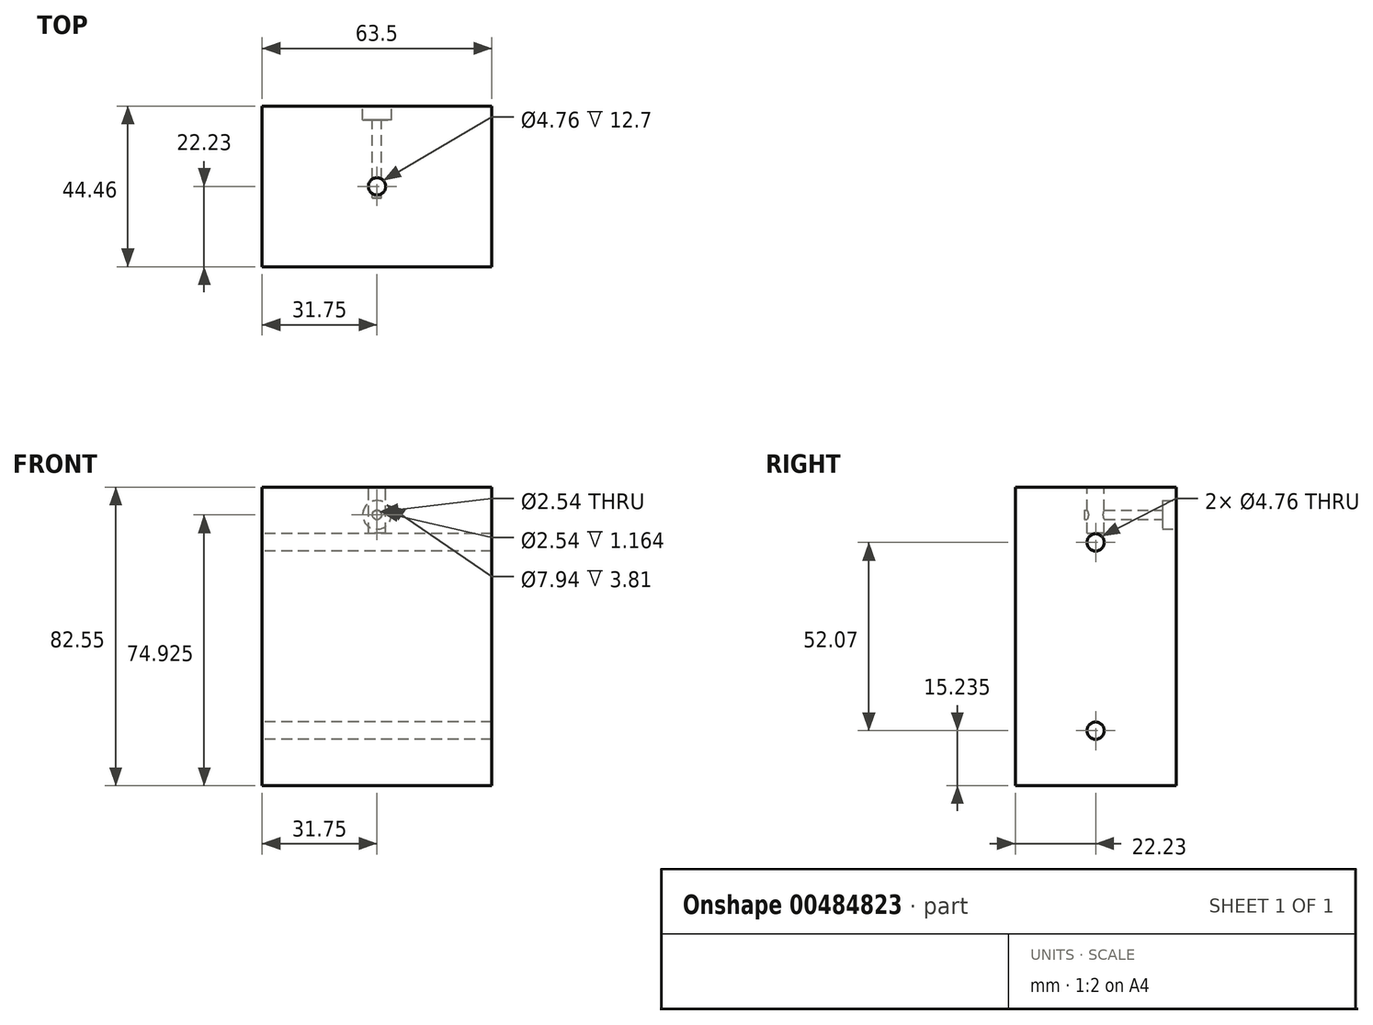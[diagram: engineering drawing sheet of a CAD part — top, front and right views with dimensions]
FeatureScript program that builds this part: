
annotation { "Feature Type Name" : "Feature", "Feature Type Description" : "" }
export const myFeature = defineFeature(function(context is Context, id is Id, definition is map)
    precondition{}
    {
        {
            var Q0;
            Q0=qCreatedBy(makeId("Front.planeOp"),FACE);
            var sketch = newSketch(context, id + "F0", { "sketchPlane" : qUnion([Q0])});
            skLineSegment(sketch, "E0.bottom", {"start": v(-31.75, 41.28) * mm, "end": v(31.75, 41.28) * mm});
            skLineSegment(sketch, "E0.top", {"start": v(-31.75, -41.28) * mm, "end": v(31.75, -41.28) * mm});
            skLineSegment(sketch, "E0.left", {"start": v(-31.75, 41.27) * mm, "end": v(-31.75, -41.27) * mm});
            skLineSegment(sketch, "E0.right", {"start": v(31.75, 41.28) * mm, "end": v(31.75, -41.27) * mm});
            skSolve(sketch);
        }
        {
            var Q0;
            Q0 = qSketchRegion(id + "F0", true);
            extrude(context, id + "F1", {"entities" : qUnion([Q0]), "depth" : 44.45 * mm, "symmetric" : true});
        }
        {
            var Q0;
            Q0=makeQuery(id+"F1.opExtrude","SWEPT_FACE",FACE,{"disambiguationData":[OSD([sQuery(id+"F0.wireOp",EDGE,"E0.bottom")])]});
            var sketch = newSketch(context, id + "F2", { "sketchPlane" : qUnion([Q0])});
            skCircle(sketch, "E1", {"center": v(0, 0) * mm, "radius": 2.38 * mm});
            skSolve(sketch);
        }
        {
            var Q0;
            Q0 = qSketchRegion(id + "F2", true);
            extrude(context, id + "F3", {"entities" : qUnion([Q0]), "operationType" : NewBodyOperationType.REMOVE, "oppositeDirection" : true, "depth" : 12.7 * mm});
        }
        {
            var Q0;
            Q0=makeQuery(id+"F1.opExtrude","SWEPT_FACE",FACE,{"disambiguationData":[OSD([sQuery(id+"F0.wireOp",EDGE,"E0.left")])]});
            var sketch = newSketch(context, id + "F4", { "sketchPlane" : qUnion([Q0])});
            skCircle(sketch, "E2", {"center": v(0, 26.04) * mm, "radius": 2.38 * mm});
            skCircle(sketch, "E3", {"center": v(0, -26.04) * mm, "radius": 2.38 * mm});
            skSolve(sketch);
        }
        {
            var Q0;
            Q0 = qSketchRegion(id + "F4", true);
            extrude(context, id + "F5", {"entities" : qUnion([Q0]), "operationType" : NewBodyOperationType.REMOVE, "endBound" : BoundingType.THROUGH_ALL, "oppositeDirection" : true, "depth" : 25.4 * mm});
        }
        {
            var Q0;
            Q0=makeQuery(id+"F1.opExtrude","CAP_FACE",FACE,{"disambiguationData":[OSD([sQuery(id+"F0.wireOp",EDGE,"E0.bottom"),sQuery(id+"F0.wireOp",EDGE,"E0.top"),sQuery(id+"F0.wireOp",EDGE,"E0.left"),sQuery(id+"F0.wireOp",EDGE,"E0.right")])],"isStart":true});
            var sketch = newSketch(context, id + "F6", { "sketchPlane" : qUnion([Q0])});
            skCircle(sketch, "E4", {"center": v(0, 33.66) * mm, "radius": 1.27 * mm});
            skSolve(sketch);
        }
        {
            var Q0;
            Q0 = qSketchRegion(id + "F6", true);
            extrude(context, id + "F7", {"entities" : qUnion([Q0]), "operationType" : NewBodyOperationType.REMOVE, "oppositeDirection" : true, "depth" : 25.4 * mm});
        }
        {
            var Q0;
            Q0=makeQuery(id+"F1.opExtrude","CAP_FACE",FACE,{"disambiguationData":[OSD([sQuery(id+"F0.wireOp",EDGE,"E0.bottom"),sQuery(id+"F0.wireOp",EDGE,"E0.top"),sQuery(id+"F0.wireOp",EDGE,"E0.left"),sQuery(id+"F0.wireOp",EDGE,"E0.right")])],"isStart":true});
            var sketch = newSketch(context, id + "F8", { "sketchPlane" : qUnion([Q0])});
            skCircle(sketch, "E5", {"center": v(0, 33.66) * mm, "radius": 3.97 * mm});
            skSolve(sketch);
        }
        {
            var Q0;
            Q0 = qSketchRegion(id + "F8", true);
            extrude(context, id + "F9", {"entities" : qUnion([Q0]), "operationType" : NewBodyOperationType.REMOVE, "oppositeDirection" : true, "depth" : 3.8 * mm});
        }
    });
